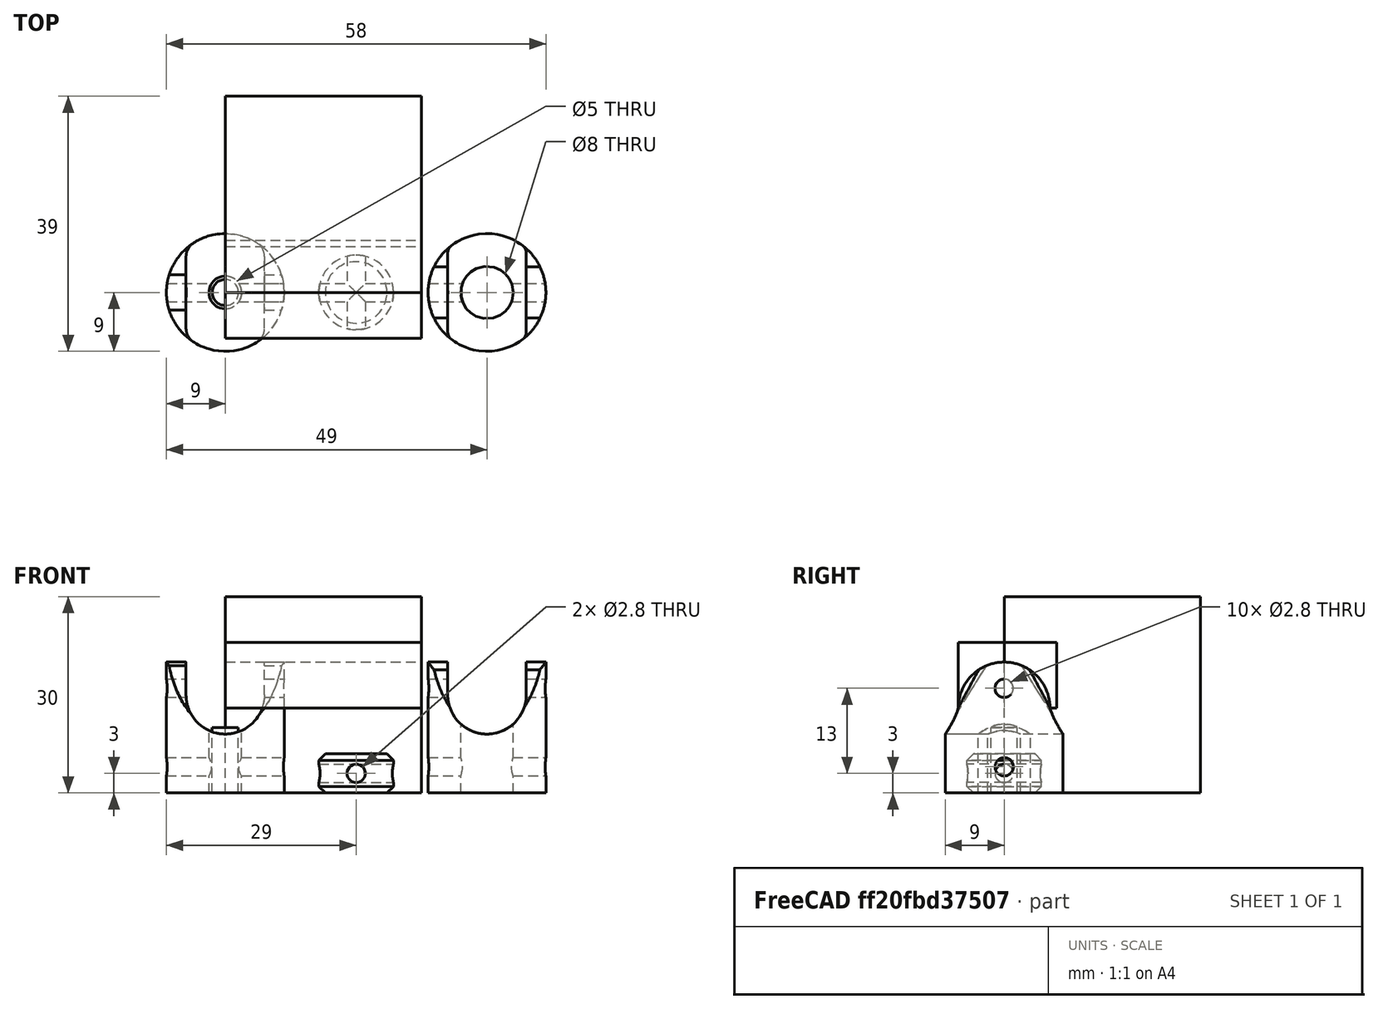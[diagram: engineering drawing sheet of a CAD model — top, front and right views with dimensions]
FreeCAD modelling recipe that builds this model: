
FCSTD DOCUMENT  (FreeCAD 0.14R3700 (Git))
Label: unijoint_v2
License: CC-BY 3.0
LicenseURL: http://creativecommons.org/licenses/by/3.0/
objects: Part::Cylinder×15, Part::Cut×8, Part::Box×6, Part::MultiFuse×5, Part::Feature×4, Part::Chamfer×1
note: 39 computed .brp shape members not serialized (recipe doc carries the construction recipe); baked Part::Feature solids carry a one-line shape summary decoded from their .brp

FEATURE [Part::Cylinder] Cylinder001  label="cyl cutout joiner 5"
  Angle = 360
  Height = 20
  Placement = pos=(0,10,15) rot=(1,0,0;1.5708rad)
  Radius = 6
FEATURE [Part::Box] Box  label="cube cutout for joiner 5"
  Height = 10
  Length = 12
  Placement = pos=(-6,-10,15) rot=(0,0,1;0rad)
  Width = 20
FEATURE [Part::Cylinder] Cylinder002  label="Base 8"
  Angle = 360
  Height = 20
  Radius = 9
FEATURE [Part::Cylinder] Cylinder003  label="joiner pin holes 5"
  Angle = 360
  Height = 22
  Placement = pos=(-11,0,16) rot=(0,1,0;1.5708rad)
  Radius = 1.4
FEATURE [Part::Cylinder] Cylinder004  label="joiner base"
  Angle = 360
  Height = 6
  Radius = 5.7
FEATURE [Part::Cylinder] Cylinder005  label="joiner pin 1"
  Angle = 360
  Height = 18
  Placement = pos=(0,9,3) rot=(1,0,0;1.5708rad)
  Radius = 1.4
FEATURE [Part::Cylinder] Cylinder007  label="5mm"
  Angle = 360
  Height = 12
  Placement = pos=(0,0,-0.5) rot=(0,0,1;0rad)
  Radius = 2.5
FEATURE [Part::Cylinder] Cylinder008  label="locking pin 5"
  Angle = 360
  Height = 20
  Placement = pos=(-10,0,4) rot=(0,1,0;1.5708rad)
  Radius = 1.4
FEATURE [Part::Cylinder] Cylinder  label="Base 5"
  Angle = 360
  Height = 20
  Radius = 9
FEATURE [Part::Cylinder] Cylinder012  label="joiner pin 2"
  Angle = 360
  Height = 18
  Placement = pos=(-9,0,3) rot=(0,1,0;1.5708rad)
  Radius = 1.4
FEATURE [Part::MultiFuse] Fusion002  label="joiner pins"
  Shapes = -> [Cylinder012,Cylinder005]
FEATURE [Part::Cut] Cut009
  Base = -> Cylinder004
  Tool = -> Fusion002
FEATURE [Part::Chamfer] Chamfer  label="joiner"
  Base = -> Cut009
  Edges = 2 edges r=1: [Edge4,Edge6]
  Placement = pos=(20,0,0) rot=(0,0,1;0rad)
FEATURE [Part::MultiFuse] Fusion  label="cutouts"
  Shapes = -> [Cylinder003,Cylinder008,Cylinder001,Box]
FEATURE [Part::Box] Box001  label="cube cutout for joiner 006"
  Height = 10
  Length = 12
  Placement = pos=(-6,-10,15) rot=(0,0,1;0rad)
  Width = 20
FEATURE [Part::Cylinder] Cylinder013  label="cyl cutout joiner 006"
  Angle = 360
  Height = 20
  Placement = pos=(0,10,15) rot=(1,0,0;1.5708rad)
  Radius = 6
FEATURE [Part::Cylinder] Cylinder014  label="locking pin 006"
  Angle = 360
  Height = 20
  Placement = pos=(-10,0,4) rot=(0,1,0;1.5708rad)
  Radius = 1.4
FEATURE [Part::Cylinder] Cylinder015  label="joiner pin holes 006"
  Angle = 360
  Height = 22
  Placement = pos=(-11,0,16) rot=(0,1,0;1.5708rad)
  Radius = 1.4
FEATURE [Part::MultiFuse] Fusion003  label="cutouts001"
  Shapes = -> [Cylinder015,Cylinder014,Cylinder013,Box001]
FEATURE [Part::Cut] Cut
  Base = -> Cylinder002
  Tool = -> Fusion
FEATURE [Part::Cut] Cut010
  Base = -> Cylinder
  Tool = -> Fusion003
FEATURE [Part::Cylinder] Cylinder016  label="5mm001"
  Angle = 360
  Height = 12
  Placement = pos=(0,0,-0.5) rot=(0,0,1;0rad)
  Radius = 4
FEATURE [Part::Cut] Cut011  label="5mm002"
  Base = -> Cut
  Tool = -> Cylinder007
FEATURE [Part::Cut] Cut012  label="8mm"
  Base = -> Cut010
  Placement = pos=(40,0,0) rot=(0,0,1;0rad)
  Tool = -> Cylinder016
FEATURE [Part::Box] Box002  label="Cube"
  Height = 30
  Length = 30
  Width = 30
FEATURE [Part::Cylinder] Cylinder017  label="Cylinder"
  Angle = 360
  Height = 10
  Radius = 2
FEATURE [Part::Cylinder] Cylinder018  label="cyl cutout joiner 007"
  Angle = 360
  Height = 30
  Placement = pos=(0,0,13) rot=(0,1,0;1.5708rad)
  Radius = 7
FEATURE [Part::Box] Box003  label="cube cutout for joiner 007"
  Height = 10
  Length = 30
  Placement = pos=(0,-7,13) rot=(0,0,1;0rad)
  Width = 15
FEATURE [Part::Cut] Cut013
  Base = -> Box003
  Tool = -> Cylinder018
FEATURE [Part::Feature] Cut013_solid  label="Cut013 (Solid)"
  Placement = pos=(25,0,0) rot=(0,0,1;0rad)
  shape: bbox 30 x 15 x 10 mm, 7 faces (baked)
FEATURE [Part::Feature] Cut013_solid001  label="Cut013 (Solid)001"
  Placement = pos=(-15,0,0) rot=(0,0,1;0rad)
  shape: bbox 30 x 15 x 10 mm, 7 faces (baked)
FEATURE [Part::Box] Box005  label="Cube002"
  Height = 15
  Length = 20
  Placement = pos=(-10,8.6,10) rot=(1,0,0;0.558505rad)
  Width = 5
FEATURE [Part::Box] Box008  label="Cube005"
  Height = 15
  Length = 20
  Placement = pos=(30,8.6,10) rot=(1,0,0;0.488692rad)
  Width = 5
FEATURE [Part::Feature] Part__Mirroring001  label="Cube005 (Mirror #1)001"
  shape: bbox 20 x 11.46 x 15.59 mm, 6 faces (baked)
FEATURE [Part::Feature] Part__Mirroring002  label="Cube002 (Mirror #1)001"
  shape: bbox 20 x 12.19 x 15.37 mm, 6 faces (baked)
FEATURE [Part::MultiFuse] Fusion004
  Shapes = -> [Part__Mirroring002,Box005,Cut013_solid001]
FEATURE [Part::MultiFuse] Fusion005
  Shapes = -> [Part__Mirroring001,Cut013_solid,Box008]
FEATURE [Part::Cut] Cut014
  Base = -> Cut012
  Tool = -> Fusion005
FEATURE [Part::Cut] Cut015
  Base = -> Cut011
  Tool = -> Fusion004
